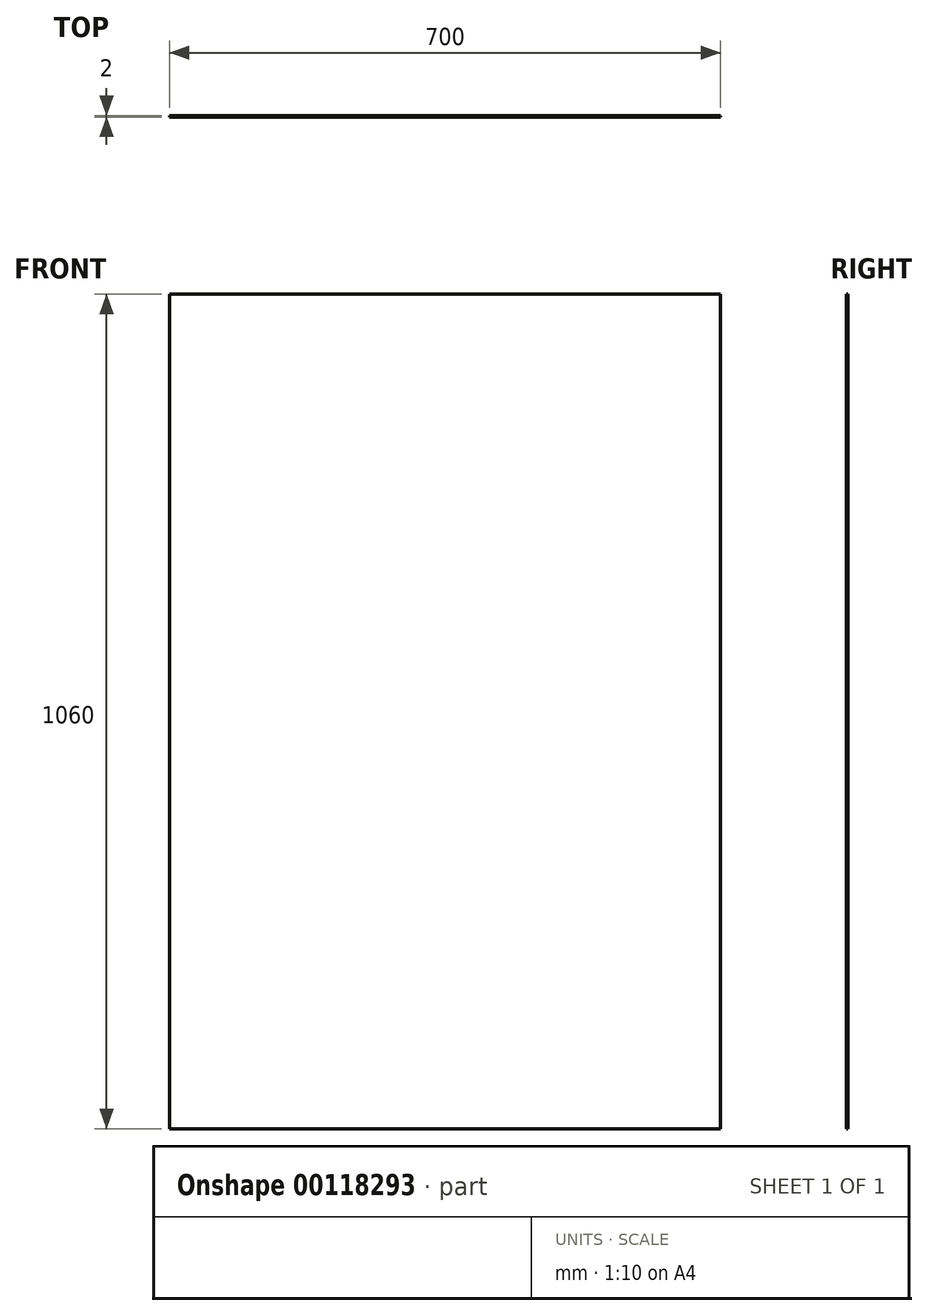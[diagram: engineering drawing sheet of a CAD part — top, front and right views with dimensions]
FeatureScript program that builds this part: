
annotation { "Feature Type Name" : "Feature", "Feature Type Description" : "" }
export const myFeature = defineFeature(function(context is Context, id is Id, definition is map)
    precondition{}
    {
        {
            var Q0;
            Q0=qCreatedBy(makeId("Front.planeOp"),FACE);
            var sketch = newSketch(context, id + "F0", { "sketchPlane" : qUnion([Q0])});
            skLineSegment(sketch, "E0.bottom", {"start": v(350, 530) * mm, "end": v(-350, 530) * mm});
            skLineSegment(sketch, "E0.top", {"start": v(350, -530) * mm, "end": v(-350, -530) * mm});
            skLineSegment(sketch, "E0.left", {"start": v(350, 530) * mm, "end": v(350, -530) * mm});
            skLineSegment(sketch, "E0.right", {"start": v(-350, 530) * mm, "end": v(-350, -530) * mm});
            skPoint(sketch, "E0.middle", {"position": v(0, 0) * mm});
            skSolve(sketch);
        }
        {
            var Q0;
            Q0=makeQuery(id+"F0.imprint","IMPRINT",FACE,{"disambiguationData":[TD([[makeQuery(id+"F0.imprint","IMPRINT",EDGE,{"derivedFrom":sQuery(id+"F0.wireOp",EDGE,"E0.bottom")}),1.0]])]});
            extrude(context, id + "F1", {"entities" : qUnion([Q0]), "depth" : 2 * mm});
        }
    });
